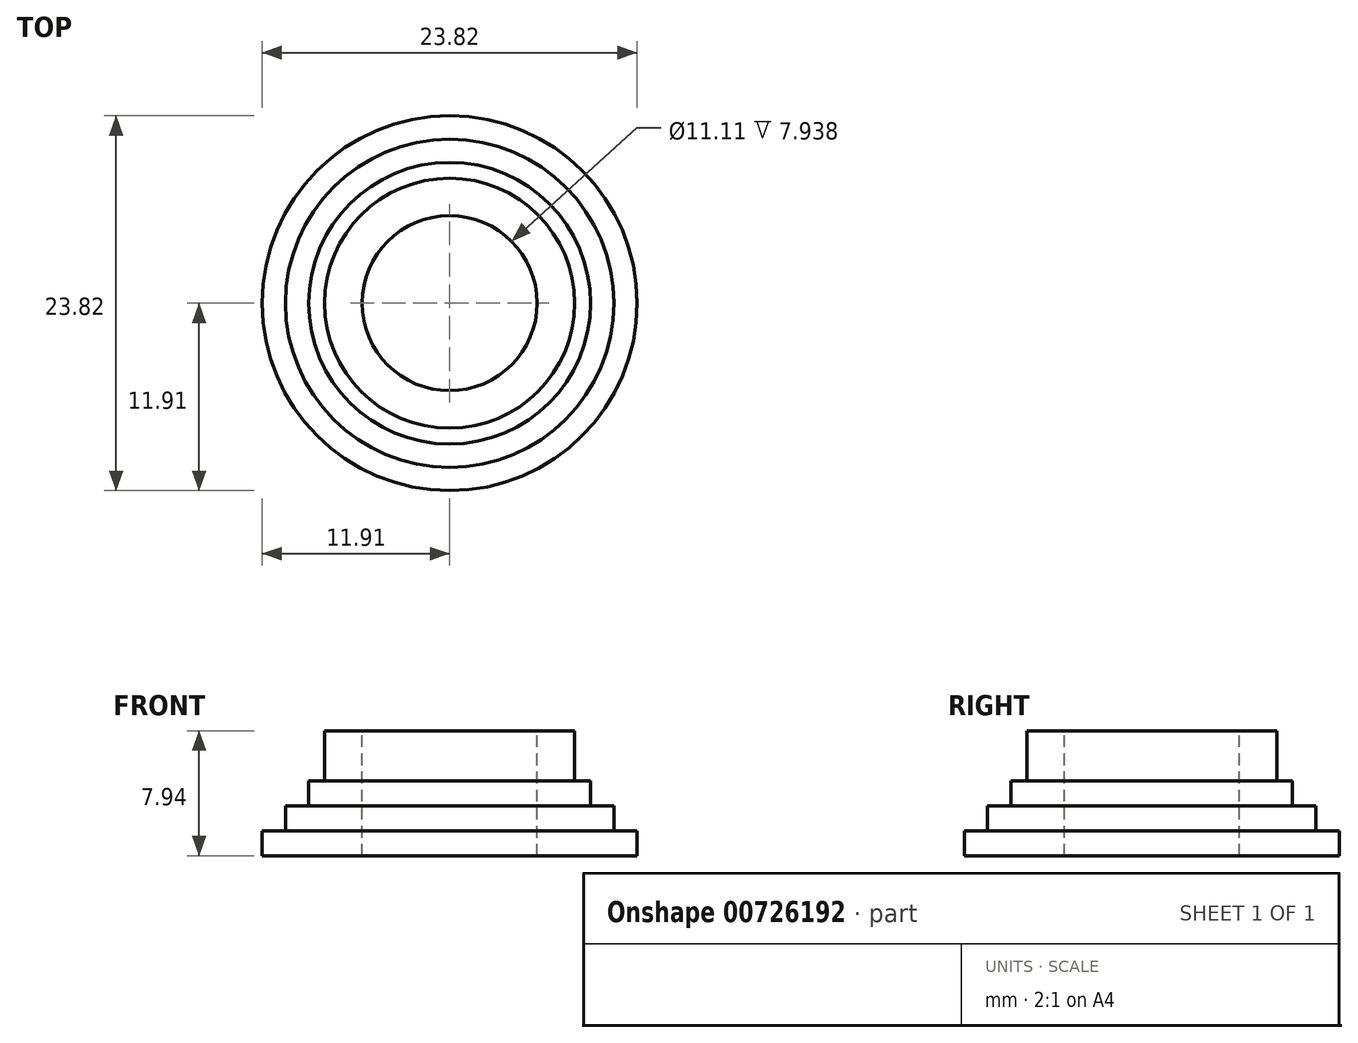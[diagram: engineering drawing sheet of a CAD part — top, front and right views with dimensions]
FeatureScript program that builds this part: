
annotation { "Feature Type Name" : "Feature", "Feature Type Description" : "" }
export const myFeature = defineFeature(function(context is Context, id is Id, definition is map)
    precondition{}
    {
        {
            var Q0;
            Q0=qCreatedBy(makeId("Front.planeOp"),FACE);
            var sketch = newSketch(context, id + "F0", { "sketchPlane" : qUnion([Q0])});
            skLineSegment(sketch, "E0", {"start": v(5.56, 0) * mm, "end": v(11.9, 0) * mm});
            skLineSegment(sketch, "E1", {"start": v(11.9, 0) * mm, "end": v(11.9, 1.59) * mm});
            skLineSegment(sketch, "E2", {"start": v(11.9, 1.59) * mm, "end": v(10.43, 1.59) * mm});
            skLineSegment(sketch, "E3", {"start": v(8.95, 3.18) * mm, "end": v(8.95, 4.76) * mm});
            skLineSegment(sketch, "E4", {"start": v(8.95, 4.76) * mm, "end": v(7.94, 4.76) * mm});
            skLineSegment(sketch, "E5", {"start": v(7.94, 4.76) * mm, "end": v(7.94, 7.94) * mm});
            skLineSegment(sketch, "E6", {"start": v(7.94, 7.94) * mm, "end": v(5.56, 7.94) * mm});
            skLineSegment(sketch, "E7", {"start": v(5.56, 7.94) * mm, "end": v(5.56, 0) * mm});
            skLineSegment(sketch, "E8", {"start": v(8.95, 3.18) * mm, "end": v(10.43, 3.18) * mm});
            skLineSegment(sketch, "E9", {"start": v(10.43, 3.18) * mm, "end": v(10.43, 1.59) * mm});
            skSolve(sketch);
        }
        {
            var Q0;
            Q0=qCreatedBy(makeId("Front.planeOp"),FACE);
            var sketch = newSketch(context, id + "F1", { "sketchPlane" : qUnion([Q0])});
            skLineSegment(sketch, "E10", {"start": v(0, 29.28) * mm, "end": v(0, -19.17) * mm, "construction": true});
            skSolve(sketch);
        }
        {
            var Q0;
            Q0=makeQuery(id+"F0.imprint","IMPRINT",FACE,{"disambiguationData":[TD([[makeQuery(id+"F0.imprint","IMPRINT",EDGE,{"derivedFrom":sQuery(id+"F0.wireOp",EDGE,"E0")}),1.0]])]});
            var Q1;
            Q1=sQuery(id+"F1.wireOp",EDGE,"E10");
            revolve(context, id + "F2", {"surfaceOperationType" : NewSurfaceOperationType.NEW, "entities" : qUnion([Q0]), "axis" : qUnion([Q1]), "revolveType" : RevolveType.FULL});
        }
    });
